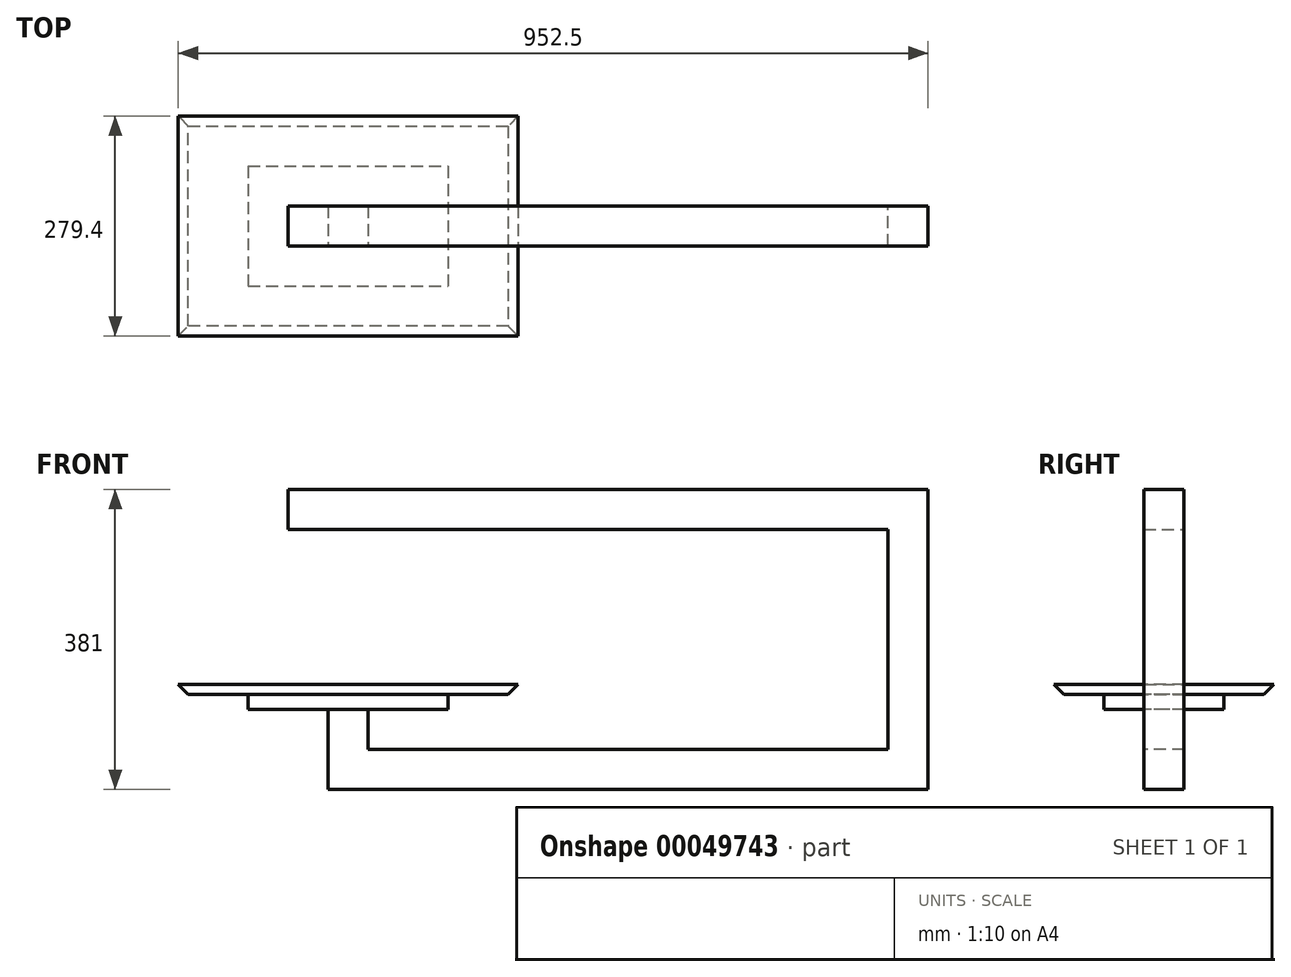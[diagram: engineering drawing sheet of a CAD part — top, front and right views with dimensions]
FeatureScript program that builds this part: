
annotation { "Feature Type Name" : "Feature", "Feature Type Description" : "" }
export const myFeature = defineFeature(function(context is Context, id is Id, definition is map)
    precondition{}
    {
        {
            var Q0;
            Q0=qCreatedBy(makeId("Front.planeOp"),FACE);
            var sketch = newSketch(context, id + "F0", { "sketchPlane" : qUnion([Q0])});
            skLineSegment(sketch, "E0.bottom", {"start": v(0, 0) * mm, "end": v(-812.8, 0) * mm});
            skLineSegment(sketch, "E0.top", {"start": v(0, -381) * mm, "end": v(-812.8, -381) * mm});
            skLineSegment(sketch, "E0.left", {"start": v(0, 0) * mm, "end": v(0, -381) * mm});
            skLineSegment(sketch, "E0.right", {"start": v(-812.8, 0) * mm, "end": v(-812.8, -381) * mm});
            skLineSegment(sketch, "E1.bottom", {"start": v(-812.8, -50.8) * mm, "end": v(-50.8, -50.8) * mm});
            skLineSegment(sketch, "E1.top", {"start": v(-812.8, -330.2) * mm, "end": v(-50.8, -330.2) * mm});
            skLineSegment(sketch, "E1.left", {"start": v(-812.8, -50.8) * mm, "end": v(-812.8, -330.2) * mm});
            skLineSegment(sketch, "E1.right", {"start": v(-50.8, -50.8) * mm, "end": v(-50.8, -330.2) * mm});
            skSolve(sketch);
        }
        {
            var Q0;
            {var subQ5=sQuery(id+"F0.wireOp",EDGE,"E0.bottom");Q0=makeQuery(id+"F0.imprint","IMPRINT",FACE,{"disambiguationData":[TD([[makeQuery(id+"F0.imprint","IMPRINT",EDGE,{"derivedFrom":subQ5}),1.0]])]});}
            extrude(context, id + "F1", {"entities" : qUnion([Q0]), "depth" : 50.8 * mm});
        }
        {
            var Q0;
            Q0=makeQuery(id+"F1.opExtrude","CAP_FACE",FACE,{"disambiguationData":[OSD([sQuery(id+"F0.wireOp",EDGE,"E0.bottom"),sQuery(id+"F0.wireOp",EDGE,"E0.top"),sQuery(id+"F0.wireOp",EDGE,"E0.left"),sQuery(id+"F0.wireOp",EDGE,"E0.right"),sQuery(id+"F0.wireOp",EDGE,"E1.bottom"),sQuery(id+"F0.wireOp",EDGE,"E1.top"),sQuery(id+"F0.wireOp",EDGE,"E1.right")])],"isStart":false});
            var sketch = newSketch(context, id + "F2", { "sketchPlane" : qUnion([Q0])});
            skLineSegment(sketch, "E2.bottom", {"start": v(-812.8, -330.2) * mm, "end": v(-762, -330.2) * mm});
            skLineSegment(sketch, "E2.top", {"start": v(-812.8, -381) * mm, "end": v(-762, -381) * mm});
            skLineSegment(sketch, "E2.left", {"start": v(-812.8, -330.2) * mm, "end": v(-812.8, -381) * mm});
            skLineSegment(sketch, "E2.right", {"start": v(-762, -330.2) * mm, "end": v(-762, -381) * mm});
            skSolve(sketch);
        }
        {
            var Q0;
            Q0=makeQuery(id+"F2.imprint","IMPRINT",FACE,{"disambiguationData":[TD([[makeQuery(id+"F2.imprint","IMPRINT",EDGE,{"derivedFrom":sQuery(id+"F2.wireOp",EDGE,"E2.bottom")}),-1.0]])]});
            extrude(context, id + "F3", {"entities" : qUnion([Q0]), "operationType" : NewBodyOperationType.REMOVE, "oppositeDirection" : true, "depth" : 50.8 * mm});
        }
        {
            var Q0;
            Q0=makeQuery(id+"F1.opExtrude","SWEPT_FACE",FACE,{"disambiguationData":[OSD([sQuery(id+"F0.wireOp",EDGE,"E1.top")])]});
            var sketch = newSketch(context, id + "F4", { "sketchPlane" : qUnion([Q0])});
            skLineSegment(sketch, "E3.bottom", {"start": v(-762, 0) * mm, "end": v(-711.2, 0) * mm});
            skLineSegment(sketch, "E3.top", {"start": v(-762, -50.8) * mm, "end": v(-711.2, -50.8) * mm});
            skLineSegment(sketch, "E3.left", {"start": v(-762, 0) * mm, "end": v(-762, -50.8) * mm});
            skLineSegment(sketch, "E3.right", {"start": v(-711.2, 0) * mm, "end": v(-711.2, -50.8) * mm});
            skSolve(sketch);
        }
        {
            var Q0;
            Q0 = qSketchRegion(id + "F4", true);
            extrude(context, id + "F5", {"entities" : qUnion([Q0]), "operationType" : NewBodyOperationType.ADD, "depth" : 50.8 * mm});
        }
        {
            var Q0;
            Q0=makeQuery(id+"F5.opExtrude","CAP_FACE",FACE,{"disambiguationData":[OSD([sQuery(id+"F4.wireOp",EDGE,"E3.bottom"),sQuery(id+"F4.wireOp",EDGE,"E3.top"),sQuery(id+"F4.wireOp",EDGE,"E3.left"),sQuery(id+"F4.wireOp",EDGE,"E3.right")])],"isStart":false});
            var sketch = newSketch(context, id + "F6", { "sketchPlane" : qUnion([Q0])});
            skLineSegment(sketch, "E4.bottom", {"start": v(-863.6, 50.8) * mm, "end": v(-609.6, 50.8) * mm});
            skLineSegment(sketch, "E4.top", {"start": v(-863.6, -101.6) * mm, "end": v(-609.6, -101.6) * mm});
            skLineSegment(sketch, "E4.left", {"start": v(-863.6, 50.8) * mm, "end": v(-863.6, -101.6) * mm});
            skLineSegment(sketch, "E4.right", {"start": v(-609.6, 50.8) * mm, "end": v(-609.6, -101.6) * mm});
            skSolve(sketch);
        }
        {
            var Q0;
            Q0=makeQuery(id+"F6.imprint","IMPRINT",FACE,{"disambiguationData":[TD([[makeQuery(id+"F6.imprint","IMPRINT",EDGE,{"derivedFrom":sQuery(id+"F6.wireOp",EDGE,"E4.bottom")}),-1.0]])]});
            var Q1;
            Q1=makeQuery(id+"F6.imprint","IMPRINT",FACE,{"disambiguationData":[TD([[makeQuery(id+"F6.imprint","IMPRINT",EDGE,{"derivedFrom":makeQuery(id+"F5.opExtrude","CAP_EDGE",EDGE,{"disambiguationData":[OSD([sQuery(id+"F4.wireOp",EDGE,"E3.bottom")])],"isStart":false})}),-1.0]])]});
            extrude(context, id + "F7", {"entities" : qUnion([Q0, Q1]), "depth" : 19.05 * mm});
        }
        {
            var Q0;
            Q0=makeQuery(id+"F7.opExtrude","CAP_FACE",FACE,{"disambiguationData":[OSD([sQuery(id+"F6.wireOp",EDGE,"E4.bottom"),sQuery(id+"F6.wireOp",EDGE,"E4.top"),sQuery(id+"F6.wireOp",EDGE,"E4.left"),sQuery(id+"F6.wireOp",EDGE,"E4.right")])],"isStart":false});
            var sketch = newSketch(context, id + "F8", { "sketchPlane" : qUnion([Q0])});
            skLineSegment(sketch, "E5.bottom", {"start": v(-939.8, 101.6) * mm, "end": v(-533.4, 101.6) * mm});
            skLineSegment(sketch, "E5.top", {"start": v(-939.8, -152.4) * mm, "end": v(-533.4, -152.4) * mm});
            skLineSegment(sketch, "E5.left", {"start": v(-939.8, 101.6) * mm, "end": v(-939.8, -152.4) * mm});
            skLineSegment(sketch, "E5.right", {"start": v(-533.4, 101.6) * mm, "end": v(-533.4, -152.4) * mm});
            skSolve(sketch);
        }
        {
            var Q0;
            Q0 = qSketchRegion(id + "F8", true);
            extrude(context, id + "F9", {"entities" : qUnion([Q0]), "operationType" : NewBodyOperationType.ADD, "depth" : 12.7 * mm, "hasDraft" : true, "draftAngle" : 45 * degree});
        }
    });
